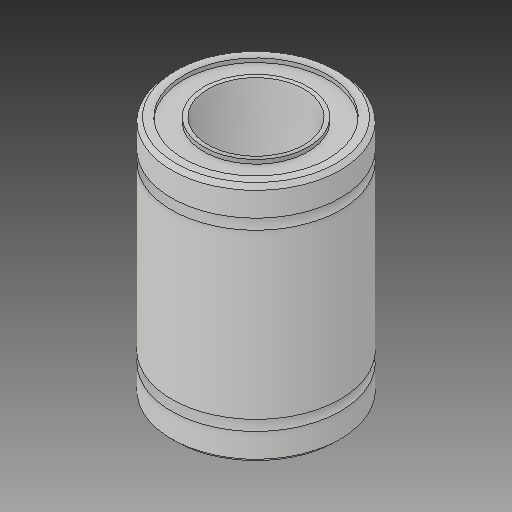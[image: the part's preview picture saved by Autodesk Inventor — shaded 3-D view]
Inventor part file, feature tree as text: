
AUTODESK INVENTOR PART (.ipt)
format: ipt  version: 2017 (Build 210142000, 142)  size: 165,888 bytes
history: native  units: mm
features: mirror x1
ambient origin geometry x8: Origin, YZ Plane, XZ Plane, XY Plane, X Axis, Y Axis, Z Axis, Center Point
bodies: Solid1 (feature_tree)
feature tree (1):
  mirror  "Mirror1"
